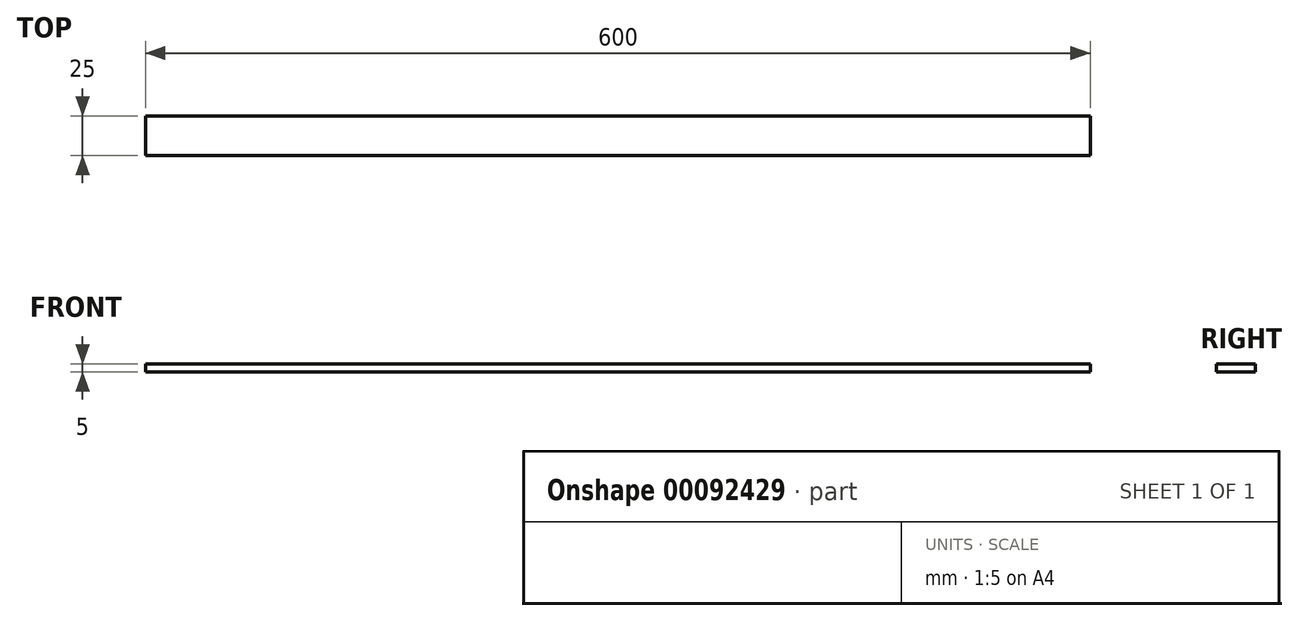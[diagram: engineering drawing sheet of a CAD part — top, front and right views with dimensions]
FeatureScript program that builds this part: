
annotation { "Feature Type Name" : "Feature", "Feature Type Description" : "" }
export const myFeature = defineFeature(function(context is Context, id is Id, definition is map)
    precondition{}
    {
        {
            var Q0;
            Q0=qCreatedBy(makeId("Front.planeOp"),FACE);
            var sketch = newSketch(context, id + "F0", { "sketchPlane" : qUnion([Q0])});
            skLineSegment(sketch, "E0", {"start": v(-374.6, 0) * mm, "end": v(225.4, 0) * mm});
            skLineSegment(sketch, "E1", {"start": v(225.4, 0) * mm, "end": v(225.4, -5) * mm});
            skLineSegment(sketch, "E2", {"start": v(225.4, -5) * mm, "end": v(-374.6, -5) * mm});
            skLineSegment(sketch, "E3", {"start": v(-374.6, -5) * mm, "end": v(-374.6, 0) * mm});
            skSolve(sketch);
        }
        {
            var Q0;
            Q0=makeQuery(id+"F0.imprint","IMPRINT",FACE,{"disambiguationData":[TD([[makeQuery(id+"F0.imprint","IMPRINT",EDGE,{"derivedFrom":sQuery(id+"F0.wireOp",EDGE,"E0")}),-1.0]])]});
            extrude(context, id + "F1", {"entities" : qUnion([Q0]), "endBound" : BoundingType.SYMMETRIC, "depth" : 25 * mm});
        }
    });
